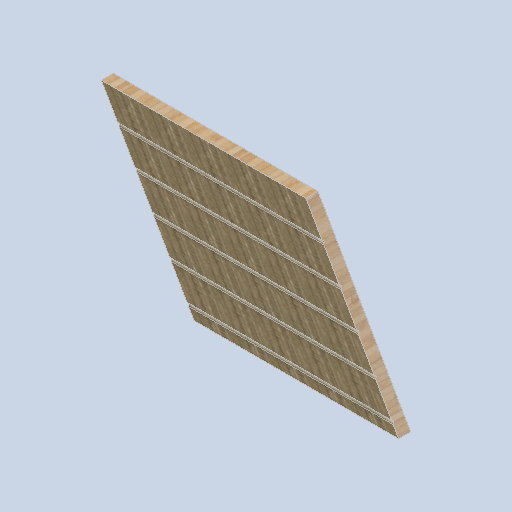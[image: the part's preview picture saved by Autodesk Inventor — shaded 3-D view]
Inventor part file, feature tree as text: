
AUTODESK INVENTOR PART (.ipt)
format: ipt  version: 2024.2 (Build 282272000, 272)  size: 226,816 bytes
history: native  units: in
note: dims shown in document units (in); Inventor stores cm internally (conversion verified against a paired STEP export)
features: other x3, sketch x2
ambient origin geometry x8: Origin, YZ Plane, XZ Plane, XY Plane, X Axis, Y Axis, Z Axis, Center Point
bodies: Solid1 (feature_tree)
feature tree (5):
  other  "side_curve_panel_02_MIR.ipt"
  other  "Solid1::side_curve_panel_02_MIR.ipt"
  other  "TaggingFeature1"
  sketch  "Sketch1"  dims[d0=0.3937in]
  sketch  "Sketch2"
